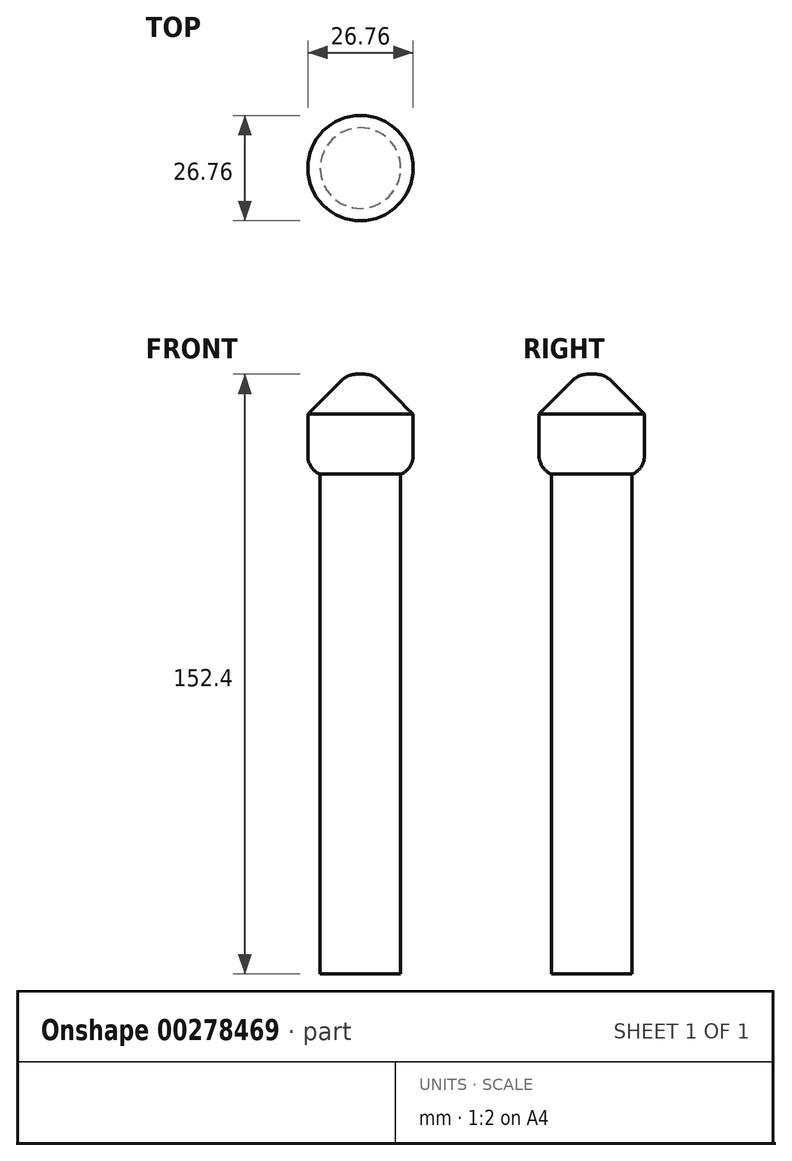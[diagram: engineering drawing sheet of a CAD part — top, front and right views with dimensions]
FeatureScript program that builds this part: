
annotation { "Feature Type Name" : "Feature", "Feature Type Description" : "" }
export const myFeature = defineFeature(function(context is Context, id is Id, definition is map)
    precondition{}
    {
        {
            var Q0;
            Q0=qCreatedBy(makeId("Top.planeOp"),FACE);
            var sketch = newSketch(context, id + "F4", { "sketchPlane" : qUnion([Q0])});
            skCircle(sketch, "E0", {"center": v(0, 0) * mm, "radius": 10.23 * mm});
            skSolve(sketch);
        }
        {
            var Q0;
            Q0 = qSketchRegion(id + "F4", true);
            extrude(context, id + "F0", {"entities" : qUnion([Q0]), "depth" : 127 * mm});
        }
        {
            var Q0;
            Q0=makeQuery(id+"F0.opExtrude","CAP_FACE",FACE,{"disambiguationData":[OSD([sQuery(id+"F4.wireOp",EDGE,"E0")])],"isStart":false});
            var sketch = newSketch(context, id + "F1", { "sketchPlane" : qUnion([Q0])});
            skCircle(sketch, "E1", {"center": v(0, 0) * mm, "radius": 13.38 * mm});
            skSolve(sketch);
        }
        {
            var Q0;
            Q0 = qSketchRegion(id + "F1", true);
            extrude(context, id + "F5", {"entities" : qUnion([Q0]), "operationType" : NewBodyOperationType.ADD, "depth" : 25.4 * mm});
        }
        {
            var Q0;
            Q0=makeQuery(id+"F5.opExtrude","CAP_EDGE",EDGE,{"disambiguationData":[OSD([sQuery(id+"F1.wireOp",EDGE,"E1")])],"isStart":true});
            fillet(context, id + "F2", {"entities" : qUnion([Q0]), "radius" : 5.08 * mm, "tangentPropagation" : true, "allowEdgeOverflow" : false});
        }
        {
            var Q0;
            Q0=makeQuery(id+"F5.opExtrude","CAP_EDGE",EDGE,{"disambiguationData":[OSD([sQuery(id+"F1.wireOp",EDGE,"E1")])],"isStart":false});
            chamfer(context, id + "F3", {"entities" : qUnion([Q0]), "width" : 10.16 * mm, "tangentPropagation" : true});
        }
        {
            var Q0;
            {var subQ0=sQuery(id+"F1.wireOp",EDGE,"E1");Q0=makeQuery(id+"F3.opChamfer","BLEND_EDGE",EDGE,{"blendedFrom":[makeQuery(id+"F5.opExtrude","CAP_EDGE",EDGE,{"disambiguationData":[OSD([subQ0])],"isStart":false}),makeQuery(id+"F5.opExtrude","CAP_FACE",FACE,{"disambiguationData":[OSD([subQ0])],"isStart":false})],"blendedInto":[makeQuery(id+"F5.opExtrude","CAP_FACE",FACE,{"disambiguationData":[OSD([subQ0])],"isStart":false})]});}
            fillet(context, id + "F6", {"entities" : qUnion([Q0]), "radius" : 5.08 * mm, "tangentPropagation" : true, "allowEdgeOverflow" : false});
        }
    });
